FCSTD DOCUMENT  (FreeCAD 1.0RUnknown)
Label: wardrobe_jan_assy4
License: All rights reserved
objects: Measure::MeasureDistance×10, App::Link×5, App::DocumentObjectGroup×4, Measure::MeasureLength×2, PartDesign::CoordinateSystem×1, App::FeaturePython×1, App::Part×1
note: 1 computed .brp shape members not serialized (recipe doc carries the construction recipe); baked Part::Feature solids carry a one-line shape summary decoded from their .brp
EXTERNAL_REF file=room_corner_chimney_left.FCStd obj=LCS_1
EXTERNAL_REF file=room_corner_chimney_left.FCStd obj=Body010
EXTERNAL_REF file=mastersketch.FCStd obj=Spreadsheet
EXTERNAL_REF file=room_corner_chimney_left.FCStd obj=LCS_inner
EXTERNAL_REF file=subassemblies/wardrobe_corpus00_jan_assy4.FCStd obj=LCS_Origin
EXTERNAL_REF file=subassemblies/wardrobe_corpus00_jan_assy4.FCStd obj=Assembly
EXTERNAL_REF file=subassemblies/wardrobe_corpus01_jan_assy4.FCStd obj=LCS_Origin
EXTERNAL_REF file=subassemblies/wardrobe_corpus01_jan_assy4.FCStd obj=Assembly
EXTERNAL_REF file=subassemblies/wardrobe_corpus02_jan_assy4.FCStd obj=LCS_Origin
EXTERNAL_REF file=subassemblies/wardrobe_corpus02_jan_assy4.FCStd obj=Assembly
EXTERNAL_REF file=subassemblies/wardrobe_corpus03_jan_assy4.FCStd obj=LCS_Origin
EXTERNAL_REF file=subassemblies/wardrobe_corpus03_jan_assy4.FCStd obj=Assembly

FEATURE [App::DocumentObjectGroup] Parts
FEATURE [PartDesign::CoordinateSystem] LCS_Origin
  AttacherType = Attacher::AttachEngine3D
  AttachmentSupport = -> [X_Axis]
  MapMode = 2
FEATURE [App::DocumentObjectGroup] Constraints
FEATURE [App::FeaturePython] Variables  # WARN: FeaturePython — macro-defined, semantics opaque (R4)
  Type = App::PropertyContainer
FEATURE [App::DocumentObjectGroup] Configurations
FEATURE [App::Link] wall
  AttachedBy = #LCS_1
  AttachedTo = Parent Assembly#LCS_Origin
  LinkPlacement = pos=(330,-1080,10) rot=(0,0,-1;1.5708rad)
  LinkedObject = -> <external room_corner_chimney_left.FCStd>#Body010
  Placement = pos=(330,-1080,10) rot=(0,0,-1;1.5708rad)
  SolverId = Asm4EE
  expr: Placement = LCS_Origin.Placement * AttachmentOffset * room_corner_chimney_left#LCS_1.Placement ^ -1
FEATURE [App::Link] wardrobe_corpus00_jan
  AttachedBy = #LCS_Origin
  AttachedTo = wall#LCS_inner
  AttachmentOffset = pos=(280,30,-320) rot=(0,-0.707107,-0.707107;3.14159rad)
  LinkPlacement = pos=(10,-800,40) rot=(0,0,-1;1.5708rad)
  LinkedObject = -> <external subassemblies/wardrobe_corpus00_jan_assy4.FCStd>#Assembly
  Placement = pos=(10,-800,40) rot=(0,0,-1;1.5708rad)
  SolverId = Asm4EE
  expr: .AttachmentOffset.Base.x = mastersketch#Spreadsheet.corpus_width / 2 + 10
  expr: .AttachmentOffset.Base.y = mastersketch#Spreadsheet.hettich_height
  expr: .AttachmentOffset.Base.z = (mastersketch#Spreadsheet.corpus_depth / 2 + 10) * -1 - 10
  expr: Placement = wall.Placement * room_corner_chimney_left#LCS_inner.Placement * AttachmentOffset * wardrobe_corpus00_jan_assy4#LCS_Origin.Placement ^ -1
FEATURE [App::Link] wardrobe_corpus01_jan
  AttachedBy = #LCS_Origin
  AttachedTo = wall#LCS_inner
  AttachmentOffset = pos=(820,30,-320) rot=(0,-0.707107,-0.707107;3.14159rad)
  LinkPlacement = pos=(10,-260,40) rot=(0,0,-1;1.5708rad)
  LinkedObject = -> <external subassemblies/wardrobe_corpus01_jan_assy4.FCStd>#Assembly
  Placement = pos=(10,-260,40) rot=(0,0,-1;1.5708rad)
  SolverId = Asm4EE
  expr: .AttachmentOffset.Base.x = mastersketch#Spreadsheet.corpus_width * 1.5 + 10
  expr: .AttachmentOffset.Base.y = mastersketch#Spreadsheet.hettich_height
  expr: .AttachmentOffset.Base.z = (mastersketch#Spreadsheet.corpus_depth / 2 + 10) * -1 - 10
  expr: Placement = wall.Placement * room_corner_chimney_left#LCS_inner.Placement * AttachmentOffset * wardrobe_corpus01_jan_assy4#LCS_Origin.Placement ^ -1
FEATURE [App::Link] wardrobe_corpus02_jan
  AttachedBy = #LCS_Origin
  AttachedTo = wall#LCS_inner
  AttachmentOffset = pos=(1360,30,-320) rot=(0,-0.707107,-0.707107;3.14159rad)
  LinkPlacement = pos=(10,280,40) rot=(0,0,-1;1.5708rad)
  LinkedObject = -> <external subassemblies/wardrobe_corpus02_jan_assy4.FCStd>#Assembly
  Placement = pos=(10,280,40) rot=(0,0,-1;1.5708rad)
  SolverId = Asm4EE
  expr: .AttachmentOffset.Base.x = mastersketch#Spreadsheet.corpus_width * 2.5 + 10
  expr: .AttachmentOffset.Base.y = mastersketch#Spreadsheet.hettich_height
  expr: .AttachmentOffset.Base.z = (mastersketch#Spreadsheet.corpus_depth / 2 + 10) * -1 - 10
  expr: Placement = wall.Placement * room_corner_chimney_left#LCS_inner.Placement * AttachmentOffset * wardrobe_corpus02_jan_assy4#LCS_Origin.Placement ^ -1
FEATURE [App::Link] wardrobe_corpus03_jan
  AttachedBy = #LCS_Origin
  AttachedTo = wall#LCS_inner
  AttachmentOffset = pos=(1890,30,-320) rot=(0,-0.707107,-0.707107;3.14159rad)
  LinkPlacement = pos=(10,810,40) rot=(0,0,-1;1.5708rad)
  LinkedObject = -> <external subassemblies/wardrobe_corpus03_jan_assy4.FCStd>#Assembly
  Placement = pos=(10,810,40) rot=(0,0,-1;1.5708rad)
  SolverId = Asm4EE
  expr: .AttachmentOffset.Base.y = mastersketch#Spreadsheet.hettich_height
  expr: Placement = wall.Placement * room_corner_chimney_left#LCS_inner.Placement * AttachmentOffset * wardrobe_corpus03_jan_assy4#LCS_Origin.Placement ^ -1
FEATURE [App::Part] Assembly  label="wardrobe_jan"
  AssemblyType = Part::Link
  Group = -> [LCS_Origin,Constraints,Variables,Configurations,wall,wardrobe_corpus00_jan,wardrobe_corpus01_jan,wardrobe_corpus02_jan,wardrobe_corpus03_jan]
  Origin = -> Origin
  Type = Assembly
FEATURE [Measure::MeasureDistance] Distance  label="Distance: 760,75 mm"
  Distance = 760.748
  DistanceX = 516
  DistanceY = 559
  DistanceZ = 9.24e-14
  Element1 = -> Assembly [wardrobe_corpus01_jan.wardrobe_door_corpus01_jan.Pad.Edge4]
  Element2 = -> Assembly [wardrobe_corpus00_jan.wardrobe_door_corpus00_jan.Pad.Edge13]
  Position1 = (-309,-527.5,40)
  Position2 = (-825,-1086.5,40)
FEATURE [Measure::MeasureDistance] Distance001  label="Distance001: 6,50 mm"
  Distance = 6.5
  DistanceX = 0
  DistanceY = 6.5
  DistanceZ = 0
  Element1 = -> Assembly [wardrobe_corpus00_jan.wardrobe_door_corpus00_jan.Pad.Edge4]
  Element2 = -> Assembly [wall.Pad.Face6]
  Position1 = (-290,-1086.5,40)
  Position2 = (-290,-1080,40)
FEATURE [Measure::MeasureDistance] Distance002  label="Distance002: 5,00 mm"
  Distance = 5
  DistanceX = 1.137e-13
  DistanceY = 5
  DistanceZ = 5.68e-14
  Element1 = -> Assembly [wardrobe_corpus02_jan.wardrobe_door_corpus02_jan.Pad.Edge4]
  Element2 = -> Assembly [wardrobe_corpus01_jan.wardrobe_door_corpus01_jan.Pad.Edge10]
  Position1 = (-309,12.5,40)
  Position2 = (-309,7.5,40)
FEATURE [Measure::MeasureLength] Length  label="Length: 2045,55 mm"
  Elements = -> [Assembly]
  Length = 2045.55
FEATURE [Measure::MeasureDistance] Distance003  label="Distance003: 535,00 mm"
  Distance = 535
  DistanceX = 535
  DistanceY = 2.274e-13
  DistanceZ = 8.53e-14
  Element1 = -> Assembly [wardrobe_corpus00_jan.wardrobe_door_corpus00_jan.Pad.Edge13]
  Element2 = -> Assembly [wardrobe_corpus00_jan.wardrobe_door_corpus00_jan.Pad.Edge4]
  Position1 = (-825,-1086.5,40)
  Position2 = (-290,-1086.5,40)
FEATURE [Measure::MeasureDistance] Distance004  label="Distance004: 535,00 mm"
  Distance = 535
  DistanceX = 2.274e-13
  DistanceY = 535
  DistanceZ = 5.68e-14
  Element1 = -> Assembly [wardrobe_corpus01_jan.wardrobe_door_corpus01_jan.Pad.Edge10]
  Element2 = -> Assembly [wardrobe_corpus01_jan.wardrobe_door_corpus01_jan.Pad.Edge4]
  Position1 = (-309,7.5,40)
  Position2 = (-309,-527.5,40)
FEATURE [Measure::MeasureDistance] Distance005  label="Distance005: 30,00 mm"
  Distance = 30
  DistanceX = 0
  DistanceY = 0
  DistanceZ = 30
  Element1 = -> Assembly [wall.Pad.Face2]
  Element2 = -> Assembly [wardrobe_corpus01_jan.wardrobe_door_corpus01_jan.Pad.Face4]
  Position1 = (-290,7.5,10)
  Position2 = (-290,7.5,40)
FEATURE [Measure::MeasureDistance] Distance006  label="Distance006: 30,00 mm"
  Distance = 30
  DistanceX = 0
  DistanceY = 0
  DistanceZ = 30
  Element1 = -> Assembly [wall.Pad.Face2]
  Element2 = -> Assembly [wardrobe_corpus00_jan.wardrobe_door_corpus00_jan.Pad.Face5]
  Position1 = (-340,-1080,10)
  Position2 = (-340,-1080,40)
FEATURE [Measure::MeasureLength] Length001  label="Length001: 2051,40 mm"
  Elements = -> [Assembly]
  Length = 2051.4
FEATURE [Measure::MeasureDistance] Distance007  label="Distance007: 257,94 mm"
  Distance = 257.938
  DistanceX = 152.892
  DistanceY = 207.5
  DistanceZ = 10
  Element1 = -> Assembly [wall.Pad.Face4]
  Element2 = -> Assembly [wardrobe_corpus00_jan.wardrobe_door_corpus00_jan.Pad.Face3]
  Position1 = (-340,-860,2490)
  Position2 = (-492.892,-1067.5,2480)
FEATURE [Measure::MeasureDistance] Distance008  label="Distance008: 10,00 mm"
  Distance = 10
  DistanceX = 0
  DistanceY = 7.60201
  DistanceZ = 6.49688
  Element1 = -> Assembly [wall.Pad.Face4]
  Element2 = -> Assembly [wardrobe_corpus01_jan.wardrobe_door_corpus01_jan.Pad.Face2]
  Position1 = (-290,15.102,1466.04)
  Position2 = (-290,7.5,1459.54)
FEATURE [Measure::MeasureDistance] Distance009  label="Distance009: 10,00 mm"
  Distance = 10
  DistanceX = 0
  DistanceY = 7.60201
  DistanceZ = 6.49688
  Element1 = -> Assembly [wall.Pad.Face4]
  Element2 = -> Assembly [wardrobe_corpus02_jan.wardrobe_door_corpus02_jan.Pad.Face2]
  Position1 = (-290,555.102,834.185)
  Position2 = (-290,547.5,827.688)
FEATURE [App::DocumentObjectGroup] Measurements
  Group = -> [Distance,Distance001,Distance002,Length,Distance003,Distance004,Distance005,Distance006,Length001,Distance007,Distance008,Distance009]

RESOLVED EXTERNAL PARTS (link-assembly join: the EXTERNAL_REF files above that resolve inside this repo's crawl, each included once):
---- part mastersketch.FCStd = doc fcstd_204cd9ce44db ----
FCSTD DOCUMENT  (FreeCAD 1.0RUnknown)
Label: mastersketch
License: All rights reserved
LicenseURL: https://en.wikipedia.org/wiki/All_rights_reserved
objects: Sketcher::SketchObject×2, PartDesign::Body×1, Spreadsheet::Sheet×1
note: 5 computed .brp shape members not serialized (recipe doc carries the construction recipe); baked Part::Feature solids carry a one-line shape summary decoded from their .brp

FEATURE [Sketcher::SketchObject] Sketch  label="doors"
  ArcFitTolerance = 1e-06
  AttachmentSupport = -> [XZ_Plane]
  FullyConstrained = true
  MakeInternals = false
  MapMode = 5
  Placement = pos=(0,0,0) rot=(1,0,0;1.5708rad)
  expr: Constraints[23] = Spreadsheet.corpus_width - 5
  expr: Constraints[33] = Spreadsheet.hettich_height
  expr: Constraints[46] = Spreadsheet.corpus_width - 5
  expr: Constraints[58] = Spreadsheet.corpus_width - 5
  sketch-geometry (29):
    g0: LineSegment StartX=0 StartY=0 StartZ=0 EndX=0 EndY=2480 EndZ=0
    g1: LineSegment StartX=0 StartY=2480 StartZ=0 EndX=-220 EndY=2480 EndZ=0
    g2: LineSegment StartX=0 StartY=0 StartZ=0 EndX=-2160 EndY=0 EndZ=0
    g3: LineSegment StartX=-2160 StartY=0 StartZ=0 EndX=-2160 EndY=210 EndZ=0
    g4: LineSegment StartX=-2160 StartY=210 StartZ=0 EndX=-220 EndY=2480 EndZ=0
    g5: LineSegment StartX=-12.5 StartY=30 StartZ=0 EndX=-12.5 EndY=2081.4 EndZ=0
    g6: LineSegment StartX=-12.5 StartY=2081.4 StartZ=0 EndX=-547.5 EndY=2081.4 EndZ=0
    g7: LineSegment StartX=-547.5 StartY=2081.4 StartZ=0 EndX=-547.5 EndY=30 EndZ=0
    g8: LineSegment StartX=-547.5 StartY=30 StartZ=0 EndX=-12.5 EndY=30 EndZ=0
    g9: LineSegment StartX=-2160 StartY=194.608 StartZ=0 EndX=-206.846 EndY=2480 EndZ=0
    g10: LineSegment StartX=-2160 StartY=30 StartZ=0 EndX=0 EndY=30 EndZ=0
    g11: LineSegment StartX=-552.5 StartY=30 StartZ=0 EndX=-552.5 EndY=1449.54 EndZ=0
    g12: LineSegment StartX=-552.5 StartY=1449.54 StartZ=0 EndX=-1087.5 EndY=1449.54 EndZ=0
    g13: LineSegment StartX=-1087.5 StartY=1449.54 StartZ=0 EndX=-1087.5 EndY=30 EndZ=0
    g14: LineSegment StartX=-1087.5 StartY=30 StartZ=0 EndX=-552.5 EndY=30 EndZ=0
    g15: LineSegment StartX=-1627.5 StartY=30 StartZ=0 EndX=-1092.5 EndY=30 EndZ=0
    g16: LineSegment StartX=-1092.5 StartY=30 StartZ=0 EndX=-1092.5 EndY=817.688 EndZ=0
    g17: LineSegment StartX=-1092.5 StartY=817.688 StartZ=0 EndX=-1627.5 EndY=817.688 EndZ=0
    g18: LineSegment StartX=-1627.5 StartY=817.688 StartZ=0 EndX=-1627.5 EndY=30 EndZ=0
    g19: LineSegment StartX=-1632.5 StartY=811.837 StartZ=0 EndX=-1632.5 EndY=30 EndZ=0
    g20: LineSegment StartX=-12.5 StartY=2081.4 StartZ=0 EndX=-12.5 EndY=2470 EndZ=0
    g21: LineSegment StartX=-552.5 StartY=1449.54 StartZ=0 EndX=-552.5 EndY=2075.55 EndZ=0
    g22: LineSegment StartX=-1092.5 StartY=817.688 StartZ=0 EndX=-1092.5 EndY=1443.69 EndZ=0
    g23: LineSegment [constr] StartX=-12.5 StartY=2470 StartZ=0 EndX=-215.392 EndY=2470 EndZ=0
    g24: LineSegment [constr] StartX=-2147.5 StartY=209.234 StartZ=0 EndX=-2147.5 EndY=30 EndZ=0
    g25: LineSegment [constr] StartX=-2150 StartY=177.064 StartZ=0 EndX=-1627.5 EndY=788.443 EndZ=0
    g26: LineSegment [constr] StartX=-1904.57 StartY=493.489 StartZ=0 EndX=-1890.12 EndY=481.145 EndZ=0
    g27: LineSegment [constr] StartX=-2147.5 StartY=49 StartZ=0 EndX=-1627.5 EndY=49 EndZ=0
    g28: LineSegment [constr] StartX=-2150 StartY=177.064 StartZ=0 EndX=-2150 EndY=49 EndZ=0
  constraints (107):
    c: Distance(g0) = 2480
    c: Coincident(g0,g-1)
    c: PointOnObject(g0,g-2)
    c: Distance(g1) = 220
    c: Coincident(g1,g0)
    c: Horizontal(g1)
    c: Distance(g2) = 2160
    c: Coincident(g2,g0)
    c: PointOnObject(g2,g-1)
    c: Distance(g3) = 210
    c: Coincident(g3,g2)
    c: Vertical(g3)
    c: Coincident(g4,g3)
    c: Coincident(g4,g1)
    c: Coincident(g5,g6)
    c: Coincident(g6,g7)
    c: Coincident(g7,g8)
    c: Coincident(g8,g5)
    c: Vertical(g5)
    c: Vertical(g7)
    c: Horizontal(g6)
    c: Horizontal(g8)
    c: Distance(g0,g5) = 12.5
    c: DistanceX(g6,g6) = 535
    c: DistanceY(g5,g5) = 2051.4  'corpus00_height'
    c: PointOnObject(g9,g3)
    c: PointOnObject(g9,g1)
    c: Parallel(g4,g9)
    c: Distance(g3,g9) = 10
    c: PointOnObject(g6,g9)
    c: PointOnObject(g10,g3)
    c: PointOnObject(g10,g0)
    c: Horizontal(g10)
    c: Distance(g2,g10) = 30
    c: PointOnObject(g7,g10)
    c: Coincident(g11,g12)
    c: Coincident(g12,g13)
    c: Coincident(g13,g14)
    c: Coincident(g14,g11)
    c: Vertical(g11)
    c: Vertical(g13)
    c: Horizontal(g12)
    c: Horizontal(g14)
    c: PointOnObject(g11,g10)
    c: PointOnObject(g12,g9)
    c: Distance(g7,g11) = 5
    c: DistanceX(g12,g12) = 535
    c: Distance(g10,g12) = 1419.54  'corpus01_height'
    c: Coincident(g15,g16)
    c: Coincident(g16,g17)
    c: Coincident(g17,g18)
    c: Coincident(g18,g15)
    c: Horizontal(g15)
    c: Horizontal(g17)
    c: Vertical(g16)
    c: Vertical(g18)
    c: PointOnObject(g15,g10)
    c: PointOnObject(g17,g9)
    c: Distance(g16,g18) = 535
    c: Distance(g10,g17) = 787.688  'corpus02_height'
    c: Distance(g13,g16) = 5
    c: PointOnObject(g19,g9)
    c: PointOnObject(g19,g10)
    c: Vertical(g19)
    c: Distance(g18,g19) = 5
    c: DistanceY(g19,g19) = 781.837  'corpus03_door_height'
    c: Coincident(g20,g5)
    c: Vertical(g20)
    c: Distance(g20,g1) = 10
    c: Distance(g20,g8) = 2440  'corpus00_door_height'
    c: Coincident(g21,g11)
    c: Vertical(g21)
    c: Distance(g21,g10) = 2045.55  'corpus01_door_height'
    c: Coincident(g22,g16)
    c: Vertical(g22)
    c: PointOnObject(g21,g9)
    c: PointOnObject(g22,g9)
    c: Distance(g22,g10) = 1413.69  'corpus02_door_height'
    c: Angle(g3,g4) = 2.43442  'alpha'
    c: Distance(g6,g8) = 2051.4
    c: Coincident(g23,g20)
    c: PointOnObject(g23,g9)
    c: Horizontal(g23)
    c: DistanceX(g23,g23) = 202.892  'corpus00_door_top'
    c: PointOnObject(g24,g10)
    c: Vertical(g24)
    c: Distance(g3,g24) = 12.5
    c: Distance(g19,g24) = 515  'corpus03_door_width'
    c: PointOnObject(g25,g18)
    c: Parallel(g25,g9)
    c: PointOnObject(g26,g9)
    c: PointOnObject(g26,g25)
    c: Perpendicular(g25,g26)
    c: Distance(g26,g25) = 400
    c: Distance(g26,g26) = 19
    c: Distance(g25,g25) = 804.233  'corpus03_top'
    c: PointOnObject(g27,g24)
    c: PointOnObject(g27,g18)
    c: Horizontal(g27)
    c: Distance(g10,g27) = 19
    c: DistanceY(g27,g25) = 739.443  'corpus03_right_height'
    c: Vertical(g28)
    c: Horizontal(g28,g27)
    c: Distance(g28,g3) = 10
    c: DistanceY(g28,g28) = 128.064  'corpus03_left_height'
    c: Coincident(g28,g25)
    c: PointOnObject(g24,g9)
FEATURE [Sketcher::SketchObject] Sketch001  label="corpus"
  ArcFitTolerance = 1e-06
  AttachmentOffset = pos=(0,0,-20) rot=(0,0,1;0rad)
  AttachmentSupport = -> [XZ_Plane]
  ExternalGeometry = -> [Sketch]
  FullyConstrained = true
  MakeInternals = false
  MapMode = 5
  Placement = pos=(0,20,-4.4e-15) rot=(1,0,0;1.5708rad)
  expr: Constraints[22] = .Constraints.corpus_width
  expr: Constraints[33] = .Constraints.corpus_width
  expr: Constraints[55] = <<doors>>.Constraints.alpha
  expr: Constraints[65] = <<doors>>.Constraints.alpha
  sketch-geometry (29):
    g0: LineSegment StartX=-550 StartY=2078.47 StartZ=0 EndX=-550 EndY=30 EndZ=0
    g1: LineSegment StartX=-550 StartY=30 StartZ=0 EndX=-10 EndY=30 EndZ=0
    g2: LineSegment StartX=-10 StartY=30 StartZ=0 EndX=-10 EndY=2078.47 EndZ=0
    g3: LineSegment StartX=-10 StartY=2078.47 StartZ=0 EndX=-550 EndY=2078.47 EndZ=0
    g4: LineSegment StartX=-550 StartY=30 StartZ=0 EndX=-550 EndY=1446.62 EndZ=0
    g5: LineSegment StartX=-550 StartY=1446.62 StartZ=0 EndX=-1090 EndY=1446.62 EndZ=0
    g6: LineSegment StartX=-1090 StartY=1446.62 StartZ=0 EndX=-1090 EndY=30 EndZ=0
    g7: LineSegment StartX=-1090 StartY=30 StartZ=0 EndX=-550 EndY=30 EndZ=0
    g8: LineSegment StartX=-1090 StartY=30 StartZ=0 EndX=-1090 EndY=814.763 EndZ=0
    g9: LineSegment StartX=-1090 StartY=814.763 StartZ=0 EndX=-1630 EndY=814.763 EndZ=0
    g10: LineSegment StartX=-1630 StartY=814.763 StartZ=0 EndX=-1630 EndY=30 EndZ=0
    g11: LineSegment StartX=-1630 StartY=30 StartZ=0 EndX=-1090 EndY=30 EndZ=0
    g12: LineSegment StartX=-2150 StartY=30 StartZ=0 EndX=-1630 EndY=30 EndZ=0
    g13: LineSegment StartX=-1630 StartY=30 StartZ=0 EndX=-1630 EndY=49 EndZ=0
    g14: LineSegment StartX=-1630 StartY=49 StartZ=0 EndX=-2150 EndY=49 EndZ=0
    g15: LineSegment StartX=-2150 StartY=49 StartZ=0 EndX=-2150 EndY=30 EndZ=0
    g16: LineSegment StartX=-1649 StartY=49 StartZ=0 EndX=-1630 EndY=49 EndZ=0
    g17: LineSegment StartX=-1630 StartY=49 StartZ=0 EndX=-1630 EndY=785.518 EndZ=0
    g18: LineSegment StartX=-1649 StartY=763.286 StartZ=0 EndX=-1649 EndY=49 EndZ=0
    g19: LineSegment StartX=-1630 StartY=785.518 StartZ=0 EndX=-1649 EndY=763.286 EndZ=0
    g20: LineSegment StartX=-2150 StartY=49 StartZ=0 EndX=-2131 EndY=49 EndZ=0
    g21: LineSegment StartX=-2131 StartY=49 StartZ=0 EndX=-2131 EndY=199.296 EndZ=0
    g22: LineSegment StartX=-2150 StartY=177.064 StartZ=0 EndX=-2150 EndY=49 EndZ=0
    g23: LineSegment StartX=-2131 StartY=199.296 StartZ=0 EndX=-2150 EndY=177.064 EndZ=0
    g24: LineSegment StartX=-2150 StartY=177.064 StartZ=0 EndX=-2150 EndY=206.309 EndZ=0
    g25: LineSegment StartX=-2150 StartY=206.309 StartZ=0 EndX=-1630 EndY=814.763 EndZ=0
    g26: LineSegment StartX=-1630 StartY=814.763 StartZ=0 EndX=-1630 EndY=785.518 EndZ=0
    g27: LineSegment StartX=-1630 StartY=785.518 StartZ=0 EndX=-2150 EndY=177.064 EndZ=0
    g28: LineSegment [constr] StartX=-2150 StartY=206.309 StartZ=0 EndX=-2135.56 EndY=193.965 EndZ=0
  constraints (86):
    c: Coincident(g0,g1)
    c: Coincident(g1,g2)
    c: Coincident(g2,g3)
    c: Coincident(g3,g0)
    c: Vertical(g0)
    c: Vertical(g2)
    c: Horizontal(g1)
    c: Horizontal(g3)
    c: PointOnObject(g1,g-8)
    c: Distance(g-5,g2) = 10
    c: Distance(g2,g0) = 540  'corpus_width'
    c: Coincident(g4,g5)
    c: Coincident(g5,g6)
    c: Coincident(g6,g7)
    c: Coincident(g7,g4)
    c: Vertical(g4)
    c: Vertical(g6)
    c: Horizontal(g5)
    c: Horizontal(g7)
    c: Coincident(g4,g0)
    c: PointOnObject(g0,g-9)
    c: PointOnObject(g5,g-9)
    c: DistanceX(g6,g0) = 540
    c: Coincident(g8,g9)
    c: Coincident(g9,g10)
    c: Coincident(g10,g11)
    c: Coincident(g11,g8)
    c: Vertical(g8)
    c: Vertical(g10)
    c: Horizontal(g9)
    c: Horizontal(g11)
    c: Coincident(g8,g6)
    c: PointOnObject(g9,g-9)
    c: DistanceX(g10,g6) = 540
    c: Coincident(g12,g13)
    c: Coincident(g13,g14)
    c: Coincident(g14,g15)
    c: Coincident(g15,g12)
    c: Horizontal(g12)
    c: Horizontal(g14)
    c: Vertical(g13)
    c: Vertical(g15)
    c: PointOnObject(g12,g-8)
    c: PointOnObject(g13,g10)
    c: Distance(g12,g14) = 19
    c: DistanceX(g-8,g12) = 10
    c: Coincident(g16,g17)
    c: Coincident(g18,g16)
    c: Horizontal(g16)
    c: Vertical(g17)
    c: Vertical(g18)
    c: PointOnObject(g16,g14)
    c: PointOnObject(g17,g10)
    c: Coincident(g19,g17)
    c: Coincident(g18,g19)
    c: Angle(g18,g19) = 2.43442
    c: Distance(g16,g13) = 19
    c: Coincident(g20,g21)
    c: Coincident(g22,g20)
    c: Horizontal(g20)
    c: Vertical(g21)
    c: Vertical(g22)
    c: Coincident(g20,g14)
    c: Coincident(g23,g21)
    c: Coincident(g22,g23)
    c: Angle(g22,g23) = 2.43442
    c: Distance(g14,g20) = 19
    c: Coincident(g24,g22)
    c: Vertical(g24)
    c: Coincident(g25,g24)
    c: PointOnObject(g25,g10)
    c: Coincident(g26,g25)
    c: Coincident(g26,g17)
    c: Coincident(g27,g17)
    c: Coincident(g27,g22)
    c: Parallel(g27,g25)
    c: Parallel(g25,g-9)
    c: Coincident(g28,g24)
    c: PointOnObject(g28,g23)
    c: Perpendicular(g27,g28)
    c: Distance(g28,g28) = 19
    c: PointOnObject(g25,g-9)
    c: DistanceY(g13,g17) = 736.518  'corpus03_right_height'
    c: DistanceY(g22,g22) = 128.064  'corpus03_left_height'
    c: DistanceY(g10,g9) = 784.763  'corpus03_back_height'
    c: DistanceX(g14,g10) = 520  'corpus03_width'
FEATURE [PartDesign::Body] Body
  AllowCompound = false
  Group = -> [Sketch,Sketch001]
  Origin = -> Origin
FEATURE [Spreadsheet::Sheet] Spreadsheet
  cells = A1='corpus_width; B1(corpus_width)=540; A2='corpus_depth; B2(corpus_depth)=600; A3='corpus_outer_thickness; B3(corpus_outer_thickness)=19; A4='corpus_backplate_thickness; B4(corpus_backplate_thickness)=19; A5='corpus_heigth; B5(corpus_height)=2045; A6='corpus01_heigth; B6(corpus01_height)=1415; A7='corpus02_heigth; B7(corpus02_height)=780; A8='drawer_outer_thickness; B8(drawer_outer_thickness)=19; A9='drawer_bottom_thickness; B9(drawer_bottom_thickness)=6; A10='drawer_length; B10(drawer_length)==B2 - 50; A11='drawer_width; B11(drawer_width)==B1 - 2 * 12.5 - 2 * B3; A12='drawer_bottom_tol; B12(drawer_bottom_tol)=0.5; A13='drawer_height; B13(drawer_height)=170; A14='drawer_slot_depth; B14(drawer_slot_depth)=8; A15='drawer_slot_height; B15(drawer_slot_height)=10; A16='hettich_height; B16(hettich_height)=30
---- part room_corner_chimney_left.FCStd = doc fcstd_721c1199e5e2 ----
FCSTD DOCUMENT  (FreeCAD 1.0RUnknown)
Label: room_corner_chimney_left
License: All rights reserved
LicenseURL: https://en.wikipedia.org/wiki/All_rights_reserved
objects: Sketcher::SketchObject×2, PartDesign::Pad×2, PartDesign::CoordinateSystem×2, PartDesign::Body×1
note: 13 computed .brp shape members not serialized (recipe doc carries the construction recipe); baked Part::Feature solids carry a one-line shape summary decoded from their .brp

FEATURE [Sketcher::SketchObject] Sketch010
  ArcFitTolerance = 1e-06
  AttachmentSupport = -> [XZ_Plane013]
  FullyConstrained = true
  MakeInternals = false
  MapMode = 5
  Placement = pos=(0,0,0) rot=(1,0,0;1.5708rad)
  sketch-geometry (10):
    g0: LineSegment StartX=0 StartY=0 StartZ=0 EndX=-2160 EndY=0 EndZ=0
    g1: LineSegment StartX=-2160 StartY=0 StartZ=0 EndX=-2160 EndY=210 EndZ=0
    g2: LineSegment StartX=0 StartY=0 StartZ=0 EndX=0 EndY=2480 EndZ=0
    g3: LineSegment StartX=0 StartY=2480 StartZ=0 EndX=-220 EndY=2480 EndZ=0
    g4: LineSegment StartX=-2160 StartY=210 StartZ=0 EndX=-220 EndY=2480 EndZ=0
    g5: LineSegment StartX=-2170 StartY=213.691 StartZ=0 EndX=-224.608 EndY=2490 EndZ=0
    g6: LineSegment StartX=10 StartY=2490 StartZ=0 EndX=-224.608 EndY=2490 EndZ=0
    g7: LineSegment StartX=10 StartY=-10 StartZ=0 EndX=10 EndY=2490 EndZ=0
    g8: LineSegment StartX=10 StartY=-10 StartZ=0 EndX=-2170 EndY=-10 EndZ=0
    g9: LineSegment StartX=-2170 StartY=-10 StartZ=0 EndX=-2170 EndY=213.691 EndZ=0
  constraints (23):
    c: Distance(g0) = 2160
    c: Coincident(g0,g-1)
    c: Horizontal(g0)
    c: Distance(g1) = 210
    c: Coincident(g1,g0)
    c: Vertical(g1)
    c: Distance(g2) = 2480
    c: Coincident(g2,g0)
    c: PointOnObject(g2,g-2)
    c: Distance(g3) = 220
    c: Coincident(g3,g2)
    c: Horizontal(g3)
    c: Coincident(g4,g1)
    c: Coincident(g4,g3)
    c: Coincident(g5,g6)
    c: Coincident(g5,g9)
    c: Coincident(g6,g7)
    c: Coincident(g7,g8)
    c: Coincident(g8,g9)
    c: Block(g5)
    c: Block(g6)
    c: Block(g7)
    c: Block(g8)
FEATURE [PartDesign::Pad] Pad010
  Direction = (0,-1,2e-16)
  Length = 670
  Length2 = 10
  Placement = pos=(0,0,0) rot=(1,0,0;1.5708rad)
  Profile = -> Sketch010
  ReferenceAxis = -> Sketch010 [N_Axis]
  Refine = true
  Suppressed = false
  Type = 0
FEATURE [Sketcher::SketchObject] Sketch
  ArcFitTolerance = 1e-06
  AttachmentSupport = -> [Pad010]
  ExternalGeometry = -> [Pad010]
  FullyConstrained = true
  MakeInternals = false
  MapMode = 5
  Placement = pos=(0,2.111e-13,0) rot=(-1,0,0;1.5708rad)
  sketch-geometry (5):
    g0: LineSegment StartX=10 StartY=-2490 StartZ=0 EndX=10 EndY=10 EndZ=0
    g1: LineSegment StartX=10 StartY=10 StartZ=0 EndX=-2170 EndY=10 EndZ=0
    g2: LineSegment StartX=-2170 StartY=10 StartZ=0 EndX=-2170 EndY=-213.691 EndZ=0
    g3: LineSegment StartX=-2170 StartY=-213.691 StartZ=0 EndX=-224.608 EndY=-2490 EndZ=0
    g4: LineSegment StartX=-224.608 StartY=-2490 StartZ=0 EndX=10 EndY=-2490 EndZ=0
  constraints (10):
    c: Coincident(g0,g-5)
    c: Coincident(g0,g-4)
    c: Coincident(g1,g0)
    c: Coincident(g1,g-7)
    c: Coincident(g2,g1)
    c: Coincident(g2,g-7)
    c: Coincident(g3,g2)
    c: Coincident(g3,g-6)
    c: Coincident(g4,g3)
    c: Coincident(g4,g0)
FEATURE [PartDesign::Pad] Pad
  BaseFeature = -> Pad010
  Direction = (0,1,2e-16)
  Length = 10
  Length2 = 10
  Placement = pos=(0,0,0) rot=(1,0,0;1.5708rad)
  Profile = -> Sketch
  ReferenceAxis = -> Sketch [N_Axis]
  Refine = true
  Suppressed = false
  Type = 0
FEATURE [PartDesign::CoordinateSystem] LCS_1
  AttacherType = Attacher::AttachEngine3D
  AttachmentSupport = -> [Pad]
  MapMode = 45
  Placement = pos=(-1080,-330,-10) rot=(0,0,1;1.5708rad)
FEATURE [PartDesign::CoordinateSystem] LCS_inner
  AttacherType = Attacher::AttachEngine3D
  AttachmentSupport = -> [Pad]
  MapMode = 7
  Placement = pos=(0,0,0) rot=(0,0.707107,0.707107;3.14159rad)
FEATURE [PartDesign::Body] Body010  label="wall"
  AllowCompound = false
  Group = -> [Sketch010,Pad010,Sketch,Pad,LCS_1,LCS_inner]
  Origin = -> Origin013
  Tip = -> Pad
---- part subassemblies/wardrobe_corpus00_jan_assy4.FCStd = doc fcstd_f454c633ce21 ----
FCSTD DOCUMENT  (FreeCAD 1.0RUnknown)
Label: wardrobe_corpus00_jan_assy4
License: All rights reserved
objects: App::Link×8, App::DocumentObjectGroup×3, Part::FeaturePython×3, PartDesign::CoordinateSystem×2, App::FeaturePython×1, App::Part×1
note: 5 computed .brp shape members not serialized (recipe doc carries the construction recipe); baked Part::Feature solids carry a one-line shape summary decoded from their .brp
EXTERNAL_REF file=parts/wardrobe_base_jan.FCStd obj=LCS_center
EXTERNAL_REF file=parts/wardrobe_base_jan.FCStd obj=Body
EXTERNAL_REF file=parts/wardrobe_base_jan.FCStd obj=LCS_1
EXTERNAL_REF file=parts/wardrobe_left_corpus00_jan.FCStd obj=LCS_bottom
EXTERNAL_REF file=parts/wardrobe_left_corpus00_jan.FCStd obj=Body001
EXTERNAL_REF file=parts/wardrobe_base_jan.FCStd obj=LCS_right
EXTERNAL_REF file=parts/wardrobe_right_corpus00_jan.FCStd obj=LCS_bottom
EXTERNAL_REF file=parts/wardrobe_right_corpus00_jan.FCStd obj=Body002
EXTERNAL_REF file=parts/wardrobe_left_corpus00_jan.FCStd obj=LCS_top
EXTERNAL_REF file=parts/wardrobe_top_jan.FCStd obj=LCS_left
EXTERNAL_REF file=parts/wardrobe_top_jan.FCStd obj=Body003
EXTERNAL_REF file=parts/wardrobe_backplate_corpus00_jan.FCStd obj=LCS_bottom
EXTERNAL_REF file=parts/wardrobe_base_jan.FCStd obj=LCS_back
EXTERNAL_REF file=parts/wardrobe_backplate_corpus00_jan.FCStd obj=Body004
EXTERNAL_REF file=parts/wardrobe_base_jan.FCStd obj=LCS_door
EXTERNAL_REF file=parts/wardrobe_door_corpus00_jan.FCStd obj=Body
EXTERNAL_REF file=wardrobe_drawer_jan_assy4.FCStd obj=LCS_Origin
EXTERNAL_REF file=parts/wardrobe_left_corpus00_jan.FCStd obj=LCS_inner_bottom
EXTERNAL_REF file=wardrobe_drawer_jan_assy4.FCStd obj=Assembly
EXTERNAL_REF file=../purchased parts/hettich-level-adjustment.FCStd obj=LCS_Origin
EXTERNAL_REF file=parts/wardrobe_base_jan.FCStd obj=LCS_2
EXTERNAL_REF file=../purchased parts/hettich-level-adjustment.FCStd obj=hettich_level_adjustment

FEATURE [App::DocumentObjectGroup] Parts
FEATURE [PartDesign::CoordinateSystem] LCS_Origin
  AttacherType = Attacher::AttachEngine3D
  AttachmentSupport = -> [X_Axis]
  MapMode = 2
FEATURE [App::DocumentObjectGroup] Constraints
FEATURE [App::FeaturePython] Variables  # WARN: FeaturePython — macro-defined, semantics opaque (R4)
  Type = App::PropertyContainer
FEATURE [App::DocumentObjectGroup] Configurations
FEATURE [App::Link] wardrobe_base_jan
  AttachedBy = #LCS_center
  AttachedTo = Parent Assembly#LCS_Origin
  LinkedObject = -> <external parts/wardrobe_base_jan.FCStd>#Body
  SolverId = Asm4EE
  expr: Placement = LCS_Origin.Placement * AttachmentOffset * wardrobe_base_jan#LCS_center.Placement ^ -1
FEATURE [App::Link] wardrobe_left_corpus00_jan
  AttachedBy = #LCS_bottom
  AttachedTo = wardrobe_base_jan#LCS_1
  LinkPlacement = pos=(-270,2.37e-13,1022.5) rot=(0,0,1;0rad)
  LinkedObject = -> <external parts/wardrobe_left_corpus00_jan.FCStd>#Body001
  Placement = pos=(-270,2.37e-13,1022.5) rot=(0,0,1;0rad)
  SolverId = Asm4EE
  expr: Placement = wardrobe_base_jan.Placement * wardrobe_base_jan#LCS_1.Placement * AttachmentOffset * wardrobe_left_corpus00_jan#LCS_bottom.Placement ^ -1
FEATURE [App::Link] wardrobe_right_corpus00_jan
  AttachedBy = #LCS_bottom
  AttachedTo = wardrobe_base_jan#LCS_right
  LinkPlacement = pos=(251,2.086e-13,1022.5) rot=(0,0,1;0rad)
  LinkedObject = -> <external parts/wardrobe_right_corpus00_jan.FCStd>#Body002
  Placement = pos=(251,2.086e-13,1022.5) rot=(0,0,1;0rad)
  SolverId = Asm4EE
  expr: Placement = wardrobe_base_jan.Placement * wardrobe_base_jan#LCS_right.Placement * AttachmentOffset * wardrobe_right_corpus00_jan#LCS_bottom.Placement ^ -1
FEATURE [App::Link] wardrobe_top_jan
  AttachedBy = #LCS_left
  AttachedTo = wardrobe_left_corpus00_jan#LCS_top
  LinkPlacement = pos=(-5.116e-13,3.858e-13,2026) rot=(0,0,1;0rad)
  LinkedObject = -> <external parts/wardrobe_top_jan.FCStd>#Body003
  Placement = pos=(-5.116e-13,3.858e-13,2026) rot=(0,0,1;0rad)
  SolverId = Asm4EE
  expr: Placement = wardrobe_left_corpus00_jan.Placement * wardrobe_left_corpus00_jan#LCS_top.Placement * AttachmentOffset * wardrobe_top_jan#LCS_left.Placement ^ -1
FEATURE [App::Link] wardrobe_backplate_corpus00_jan
  AttachedBy = #LCS_bottom
  AttachedTo = wardrobe_base_jan#LCS_back
  LinkPlacement = pos=(5.68e-14,319,1022.5) rot=(0,0,1;0rad)
  LinkedObject = -> <external parts/wardrobe_backplate_corpus00_jan.FCStd>#Body004
  Placement = pos=(5.68e-14,319,1022.5) rot=(0,0,1;0rad)
  SolverId = Asm4EE
  expr: Placement = wardrobe_base_jan.Placement * wardrobe_base_jan#LCS_back.Placement * AttachmentOffset * wardrobe_backplate_corpus00_jan#LCS_bottom.Placement ^ -1
FEATURE [App::Link] wardrobe_door_corpus00_jan
  AttachedBy = #LCS_right
  AttachedTo = wardrobe_base_jan#LCS_door
  AttachmentOffset = pos=(2.5,0,0) rot=(0,0,1;1.5708rad)
  LinkPlacement = pos=(267.5,-300,0) rot=(0.57735,0.57735,0.57735;2.0944rad)
  LinkedObject = -> <external parts/wardrobe_door_corpus00_jan.FCStd>#Body
  Placement = pos=(267.5,-300,0) rot=(0.57735,0.57735,0.57735;2.0944rad)
  SolverId = Asm4EE
  expr: Placement = wardrobe_base_jan.Placement * wardrobe_base_jan#LCS_door.Placement * AttachmentOffset * wardrobe_door_corpus00_jan#LCS_right.Placement ^ -1
FEATURE [App::Link] wardrobe_drawer_jan_assy4
  AttachedBy = #LCS_Origin
  AttachedTo = wardrobe_left_corpus00_jan#LCS_inner_bottom
  AttachmentOffset = pos=(0,20,0) rot=(0,0,1;1.5708rad)
  LinkPlacement = pos=(-251,2.232e-13,39) rot=(0.57735,0.57735,0.57735;4.18879rad)
  LinkedObject = -> <external wardrobe_drawer_jan_assy4.FCStd>#Assembly
  Placement = pos=(-251,2.232e-13,39) rot=(0.57735,0.57735,0.57735;4.18879rad)
  SolverId = Asm4EE
  expr: Placement = wardrobe_left_corpus00_jan.Placement * wardrobe_left_corpus00_jan#LCS_inner_bottom.Placement * AttachmentOffset * wardrobe_drawer_jan_assy4#LCS_Origin.Placement ^ -1
FEATURE [Part::FeaturePython] Linear_wardrobe_drawer_jan_assy4  # Draft array (typed FeaturePython)
  ArrayType = Linear Array
  Axis = -> Z_Axis
  AxisPlacement = pos=(0,0,0) rot=(0,0,1.73205;3.14159rad)
  Count = 6
  Index = 1
  LinearStep = 200
  PlacementList = 6 placements: arithmetic series from (-251,2.2323e-13,39) step (5.68434e-14,0,200) to (-251,2.2323e-13,1039)
  Placer = pos=(0,0,1000) rot=(0,0,1;0rad)
  ScaleList = (6) [(1,1,1),(1,1,1),(1,1,1),(1,1,1),(1,1,1),(1,1,1)]
  Scaler = 1
  ShowElement = false
  SourceObject = -> wardrobe_drawer_jan_assy4
  expr: .Placer.Base.z = LinearStep * Index
FEATURE [PartDesign::CoordinateSystem] LCS_003  label="LCS_1"
  AttacherType = Attacher::AttachEngine3D
FEATURE [App::Link] hettich_level_adjustment
  AttachedBy = #LCS_Origin
  AttachedTo = wardrobe_base_jan#LCS_2
  AttachmentOffset = pos=(0,0,0) rot=(0.707107,-0.707107,0;3.14159rad)
  LinkPlacement = pos=(-220,-230,0) rot=(0.707107,-0.707107,0;3.14159rad)
  LinkedObject = -> <external ../purchased parts/hettich-level-adjustment.FCStd>#hettich_level_adjustment
  Placement = pos=(-220,-230,0) rot=(0.707107,-0.707107,0;3.14159rad)
  SolverId = Asm4EE
  expr: Placement = wardrobe_base_jan.Placement * wardrobe_base_jan#LCS_2.Placement * AttachmentOffset * hettich_level_adjustment#LCS_Origin.Placement ^ -1
FEATURE [Part::FeaturePython] Linear_hettich_level_adjustment  # Draft array (typed FeaturePython)
  ArrayType = Linear Array
  Axis = -> X_Axis
  AxisPlacement = pos=(0,0,0) rot=(0.57735,0.57735,0.57735;2.0944rad)
  Count = 2
  Index = 1
  LinearStep = 440
  PlacementList = 2 placements: [(-220,-230,6.31089e-30),(220,-230,4.88498e-14)]
  Placer = pos=(0,0,440) rot=(0,0,1;0rad)
  ScaleList = (2) [(1,1,1),(1,1,1)]
  Scaler = 1
  ShowElement = false
  SourceObject = -> hettich_level_adjustment
  expr: .Placer.Base.z = LinearStep * Index
FEATURE [Part::FeaturePython] Linear_Linear_hettich_level_adjustment  # Draft array (typed FeaturePython)
  ArrayType = Linear Array
  Axis = -> Y_Axis
  AxisPlacement = pos=(0,0,0) rot=(1,1,1;4.18879rad)
  Count = 2
  Index = 1
  LinearStep = 460
  PlacementList = 2 placements: [(0,0,0),(5.10703e-14,460,-1.53211e-13)]
  Placer = pos=(0,0,460) rot=(0,0,1;0rad)
  ScaleList = (2) [(1,1,1),(1,1,1)]
  Scaler = 1
  ShowElement = false
  SourceObject = -> Linear_hettich_level_adjustment
  expr: .Placer.Base.z = LinearStep * Index
FEATURE [App::Part] Assembly  label="wardrobe_corpus00_jan"
  AssemblyType = Part::Link
  Group = -> [LCS_Origin,Constraints,Variables,Configurations,wardrobe_base_jan,wardrobe_left_corpus00_jan,wardrobe_right_corpus00_jan,wardrobe_top_jan,wardrobe_backplate_corpus00_jan,wardrobe_door_corpus00_jan,wardrobe_drawer_jan_assy4,Linear_wardrobe_drawer_jan_assy4,LCS_003,hettich_level_adjustment,Linear_hettich_level_adjustment,Linear_Linear_hettich_level_adjustment]
  Origin = -> Origin
  Type = Assembly
---- part subassemblies/wardrobe_corpus01_jan_assy4.FCStd = doc fcstd_6551963c7e1b ----
FCSTD DOCUMENT  (FreeCAD 1.0RUnknown)
Label: wardrobe_corpus01_jan_assy4
License: All rights reserved
objects: App::Link×8, App::DocumentObjectGroup×3, Part::FeaturePython×3, PartDesign::CoordinateSystem×1, App::FeaturePython×1, App::Part×1
note: 4 computed .brp shape members not serialized (recipe doc carries the construction recipe); baked Part::Feature solids carry a one-line shape summary decoded from their .brp
EXTERNAL_REF file=parts/wardrobe_base_jan.FCStd obj=LCS_center
EXTERNAL_REF file=parts/wardrobe_base_jan.FCStd obj=Body
EXTERNAL_REF file=parts/wardrobe_base_jan.FCStd obj=LCS_1
EXTERNAL_REF file=parts/wardrobe_left_corpus01_jan.FCStd obj=LCS_bottom
EXTERNAL_REF file=parts/wardrobe_left_corpus01_jan.FCStd obj=Body001
EXTERNAL_REF file=parts/wardrobe_base_jan.FCStd obj=LCS_right
EXTERNAL_REF file=parts/wardrobe_right_corpus01_jan.FCStd obj=LCS_bottom
EXTERNAL_REF file=parts/wardrobe_right_corpus01_jan.FCStd obj=Body002
EXTERNAL_REF file=parts/wardrobe_left_corpus01_jan.FCStd obj=LCS_top
EXTERNAL_REF file=parts/wardrobe_top_jan.FCStd obj=LCS_left
EXTERNAL_REF file=parts/wardrobe_top_jan.FCStd obj=Body003
EXTERNAL_REF file=parts/wardrobe_backplate_corpus01_jan.FCStd obj=LCS_bottom
EXTERNAL_REF file=parts/wardrobe_base_jan.FCStd obj=LCS_back
EXTERNAL_REF file=parts/wardrobe_backplate_corpus01_jan.FCStd obj=Body004
EXTERNAL_REF file=parts/wardrobe_base_jan.FCStd obj=LCS_door
EXTERNAL_REF file=parts/wardrobe_door_corpus01_jan.FCStd obj=Body
EXTERNAL_REF file=wardrobe_drawer_jan_assy4.FCStd obj=LCS_Origin
EXTERNAL_REF file=parts/wardrobe_left_corpus01_jan.FCStd obj=LCS_inner
EXTERNAL_REF file=wardrobe_drawer_jan_assy4.FCStd obj=Assembly
EXTERNAL_REF file=../purchased parts/hettich-level-adjustment.FCStd obj=LCS_Origin
EXTERNAL_REF file=parts/wardrobe_base_jan.FCStd obj=LCS_2
EXTERNAL_REF file=../purchased parts/hettich-level-adjustment.FCStd obj=hettich_level_adjustment

FEATURE [App::DocumentObjectGroup] Parts
FEATURE [PartDesign::CoordinateSystem] LCS_Origin
  AttacherType = Attacher::AttachEngine3D
  AttachmentSupport = -> [X_Axis]
  MapMode = 2
FEATURE [App::DocumentObjectGroup] Constraints
FEATURE [App::FeaturePython] Variables  # WARN: FeaturePython — macro-defined, semantics opaque (R4)
  Type = App::PropertyContainer
FEATURE [App::DocumentObjectGroup] Configurations
FEATURE [App::Link] wardrobe_base_jan
  AttachedBy = #LCS_center
  AttachedTo = Parent Assembly#LCS_Origin
  LinkedObject = -> <external parts/wardrobe_base_jan.FCStd>#Body
  SolverId = Asm4EE
  expr: Placement = LCS_Origin.Placement * AttachmentOffset * wardrobe_base_jan#LCS_center.Placement ^ -1
FEATURE [App::Link] wardrobe_left_corpus01_jan
  AttachedBy = #LCS_bottom
  AttachedTo = wardrobe_base_jan#LCS_1
  LinkPlacement = pos=(-270,1.102e-13,707.5) rot=(0,0,1;0rad)
  LinkedObject = -> <external parts/wardrobe_left_corpus01_jan.FCStd>#Body001
  Placement = pos=(-270,1.102e-13,707.5) rot=(0,0,1;0rad)
  SolverId = Asm4EE
  expr: Placement = wardrobe_base_jan.Placement * wardrobe_base_jan#LCS_1.Placement * AttachmentOffset * wardrobe_left_corpus01_jan#LCS_bottom.Placement ^ -1
FEATURE [App::Link] wardrobe_right_corpus01_jan
  AttachedBy = #LCS_bottom
  AttachedTo = wardrobe_base_jan#LCS_right
  LinkPlacement = pos=(251,8.18e-14,707.5) rot=(0,0,1;0rad)
  LinkedObject = -> <external parts/wardrobe_right_corpus01_jan.FCStd>#Body002
  Placement = pos=(251,8.18e-14,707.5) rot=(0,0,1;0rad)
  SolverId = Asm4EE
  expr: Placement = wardrobe_base_jan.Placement * wardrobe_base_jan#LCS_right.Placement * AttachmentOffset * wardrobe_right_corpus01_jan#LCS_bottom.Placement ^ -1
FEATURE [App::Link] wardrobe_top_jan
  AttachedBy = #LCS_left
  AttachedTo = wardrobe_left_corpus01_jan#LCS_top
  LinkPlacement = pos=(-3.979e-13,2.306e-13,1396) rot=(0,0,1;0rad)
  LinkedObject = -> <external parts/wardrobe_top_jan.FCStd>#Body003
  Placement = pos=(-3.979e-13,2.306e-13,1396) rot=(0,0,1;0rad)
  SolverId = Asm4EE
  expr: Placement = wardrobe_left_corpus01_jan.Placement * wardrobe_left_corpus01_jan#LCS_top.Placement * AttachmentOffset * wardrobe_top_jan#LCS_left.Placement ^ -1
FEATURE [App::Link] wardrobe_backplate_corpus01_jan
  AttachedBy = #LCS_bottom
  AttachedTo = wardrobe_base_jan#LCS_back
  AttachmentOffset = pos=(0,0,0) rot=(0,1,0;3.14159rad)
  LinkPlacement = pos=(-2.84e-14,300,707.5) rot=(0,0,1;3.14159rad)
  LinkedObject = -> <external parts/wardrobe_backplate_corpus01_jan.FCStd>#Body004
  Placement = pos=(-2.84e-14,300,707.5) rot=(0,0,1;3.14159rad)
  SolverId = Asm4EE
  expr: Placement = wardrobe_base_jan.Placement * wardrobe_base_jan#LCS_back.Placement * AttachmentOffset * wardrobe_backplate_corpus01_jan#LCS_bottom.Placement ^ -1
FEATURE [App::Link] wardrobe_door_corpus01_jan
  AttachedBy = #LCS_bottom
  AttachedTo = wardrobe_base_jan#LCS_door
  AttachmentOffset = pos=(2.5,0,0) rot=(0,0,1;3.14159rad)
  LinkPlacement = pos=(267.5,-300,0) rot=(1,0,0;1.5708rad)
  LinkedObject = -> <external parts/wardrobe_door_corpus01_jan.FCStd>#Body
  Placement = pos=(267.5,-300,0) rot=(1,0,0;1.5708rad)
  SolverId = Asm4EE
  expr: Placement = wardrobe_base_jan.Placement * wardrobe_base_jan#LCS_door.Placement * AttachmentOffset * wardrobe_door_corpus01_jan#LCS_bottom.Placement ^ -1
FEATURE [App::Link] wardrobe_drawer_jan_assy4
  AttachedBy = #LCS_Origin
  AttachedTo = wardrobe_left_corpus01_jan#LCS_inner
  AttachmentOffset = pos=(0,20,0) rot=(0,0,1;1.5708rad)
  LinkPlacement = pos=(-251,9.64e-14,39) rot=(0.57735,0.57735,0.57735;4.18879rad)
  LinkedObject = -> <external wardrobe_drawer_jan_assy4.FCStd>#Assembly
  Placement = pos=(-251,9.64e-14,39) rot=(0.57735,0.57735,0.57735;4.18879rad)
  SolverId = Asm4EE
  expr: Placement = wardrobe_left_corpus01_jan.Placement * wardrobe_left_corpus01_jan#LCS_inner.Placement * AttachmentOffset * wardrobe_drawer_jan_assy4#LCS_Origin.Placement ^ -1
FEATURE [Part::FeaturePython] Linear_wardrobe_drawer_jan_assy4  # Draft array (typed FeaturePython)
  ArrayType = Linear Array
  Axis = -> Z_Axis
  AxisPlacement = pos=(0,0,0) rot=(0,0,1.73205;3.14159rad)
  Count = 6
  Index = 1
  LinearStep = 200
  PlacementList = 6 placements: arithmetic series from (-251,9.643e-14,39) step (5.68434e-14,0,200) to (-251,9.643e-14,1039)
  Placer = pos=(0,0,1000) rot=(0,0,1;0rad)
  ScaleList = (6) [(1,1,1),(1,1,1),(1,1,1),(1,1,1),(1,1,1),(1,1,1)]
  Scaler = 1
  ShowElement = false
  SourceObject = -> wardrobe_drawer_jan_assy4
  expr: .Placer.Base.z = LinearStep * Index
FEATURE [App::Link] hettich_level_adjustment
  AttachedBy = #LCS_Origin
  AttachedTo = wardrobe_base_jan#LCS_2
  AttachmentOffset = pos=(0,0,0) rot=(0.707107,-0.707107,0;3.14159rad)
  LinkPlacement = pos=(-220,-230,0) rot=(0.707107,-0.707107,0;3.14159rad)
  LinkedObject = -> <external ../purchased parts/hettich-level-adjustment.FCStd>#hettich_level_adjustment
  Placement = pos=(-220,-230,0) rot=(0.707107,-0.707107,0;3.14159rad)
  SolverId = Asm4EE
  expr: Placement = wardrobe_base_jan.Placement * wardrobe_base_jan#LCS_2.Placement * AttachmentOffset * hettich_level_adjustment#LCS_Origin.Placement ^ -1
FEATURE [Part::FeaturePython] Linear_hettich_level_adjustment  # Draft array (typed FeaturePython)
  ArrayType = Linear Array
  Axis = -> X_Axis
  AxisPlacement = pos=(0,0,0) rot=(0.57735,0.57735,0.57735;2.0944rad)
  Count = 2
  Index = 1
  LinearStep = 440
  PlacementList = 2 placements: [(-220,-230,6.31089e-30),(220,-230,4.88498e-14)]
  Placer = pos=(0,0,440) rot=(0,0,1;0rad)
  ScaleList = (2) [(1,1,1),(1,1,1)]
  Scaler = 1
  ShowElement = false
  SourceObject = -> hettich_level_adjustment
  expr: .Placer.Base.z = LinearStep * Index
FEATURE [Part::FeaturePython] Linear_Linear_hettich_level_adjustment  # Draft array (typed FeaturePython)
  ArrayType = Linear Array
  Axis = -> Y_Axis
  AxisPlacement = pos=(0,0,0) rot=(1,1,1;4.18879rad)
  Count = 2
  Index = 1
  LinearStep = 460
  PlacementList = 2 placements: [(0,0,0),(5.10703e-14,460,-1.53211e-13)]
  Placer = pos=(0,0,460) rot=(0,0,1;0rad)
  ScaleList = (2) [(1,1,1),(1,1,1)]
  Scaler = 1
  ShowElement = false
  SourceObject = -> Linear_hettich_level_adjustment
  expr: .Placer.Base.z = LinearStep * Index
FEATURE [App::Part] Assembly  label="wardrobe_corpus01_jan"
  AssemblyType = Part::Link
  Group = -> [LCS_Origin,Constraints,Variables,Configurations,wardrobe_base_jan,wardrobe_left_corpus01_jan,wardrobe_right_corpus01_jan,wardrobe_top_jan,wardrobe_backplate_corpus01_jan,wardrobe_door_corpus01_jan,wardrobe_drawer_jan_assy4,Linear_wardrobe_drawer_jan_assy4,hettich_level_adjustment,Linear_hettich_level_adjustment,Linear_Linear_hettich_level_adjustment]
  Origin = -> Origin
  Type = Assembly
---- part subassemblies/wardrobe_corpus02_jan_assy4.FCStd = doc fcstd_7aecd55c14e2 ----
FCSTD DOCUMENT  (FreeCAD 1.0RUnknown)
Label: wardrobe_corpus02_jan_assy4
License: All rights reserved
objects: App::Link×7, App::DocumentObjectGroup×3, Part::FeaturePython×2, PartDesign::CoordinateSystem×1, App::FeaturePython×1, App::Part×1
note: 3 computed .brp shape members not serialized (recipe doc carries the construction recipe); baked Part::Feature solids carry a one-line shape summary decoded from their .brp
EXTERNAL_REF file=parts/wardrobe_base_jan.FCStd obj=LCS_center
EXTERNAL_REF file=parts/wardrobe_base_jan.FCStd obj=Body
EXTERNAL_REF file=parts/wardrobe_base_jan.FCStd obj=LCS_1
EXTERNAL_REF file=parts/wardrobe_left_corpus02_jan.FCStd obj=LCS_1
EXTERNAL_REF file=parts/wardrobe_left_corpus02_jan.FCStd obj=Body001
EXTERNAL_REF file=parts/wardrobe_base_jan.FCStd obj=LCS_right
EXTERNAL_REF file=parts/wardrobe_right_corpus02_jan.FCStd obj=LCS_1
EXTERNAL_REF file=parts/wardrobe_right_corpus02_jan.FCStd obj=Body002
EXTERNAL_REF file=parts/wardrobe_left_corpus02_jan.FCStd obj=LCS_top
EXTERNAL_REF file=parts/wardrobe_top_jan.FCStd obj=LCS_left
EXTERNAL_REF file=parts/wardrobe_top_jan.FCStd obj=Body003
EXTERNAL_REF file=parts/wardrobe_backplate_corpus02_jan.FCStd obj=LCS_1
EXTERNAL_REF file=parts/wardrobe_base_jan.FCStd obj=LCS_back
EXTERNAL_REF file=parts/wardrobe_backplate_corpus02_jan.FCStd obj=Body004
EXTERNAL_REF file=parts/wardrobe_base_jan.FCStd obj=LCS_door
EXTERNAL_REF file=parts/wardrobe_door_corpus02_jan.FCStd obj=LCS_1
EXTERNAL_REF file=parts/wardrobe_door_corpus02_jan.FCStd obj=Body
EXTERNAL_REF file=../purchased parts/hettich-level-adjustment.FCStd obj=LCS_Origin
EXTERNAL_REF file=parts/wardrobe_base_jan.FCStd obj=LCS_2
EXTERNAL_REF file=../purchased parts/hettich-level-adjustment.FCStd obj=hettich_level_adjustment

FEATURE [App::DocumentObjectGroup] Parts
FEATURE [PartDesign::CoordinateSystem] LCS_Origin
  AttacherType = Attacher::AttachEngine3D
  AttachmentSupport = -> [X_Axis]
  MapMode = 2
FEATURE [App::DocumentObjectGroup] Constraints
FEATURE [App::FeaturePython] Variables  # WARN: FeaturePython — macro-defined, semantics opaque (R4)
  Type = App::PropertyContainer
FEATURE [App::DocumentObjectGroup] Configurations
FEATURE [App::Link] wardrobe_base_jan
  AttachedBy = #LCS_center
  AttachedTo = Parent Assembly#LCS_Origin
  LinkedObject = -> <external parts/wardrobe_base_jan.FCStd>#Body
  SolverId = Asm4EE
  expr: Placement = LCS_Origin.Placement * AttachmentOffset * wardrobe_base_jan#LCS_center.Placement ^ -1
FEATURE [App::Link] wardrobe_left_corpus02_jan
  AttachedBy = #LCS_1
  AttachedTo = wardrobe_base_jan#LCS_1
  LinkPlacement = pos=(-270,1.25e-13,390) rot=(0,0,1;0rad)
  LinkedObject = -> <external parts/wardrobe_left_corpus02_jan.FCStd>#Body001
  Placement = pos=(-270,1.25e-13,390) rot=(0,0,1;0rad)
  SolverId = Asm4EE
  expr: Placement = wardrobe_base_jan.Placement * wardrobe_base_jan#LCS_1.Placement * AttachmentOffset * wardrobe_left_corpus02_jan#LCS_1.Placement ^ -1
FEATURE [App::Link] wardrobe_right_corpus02_jan
  AttachedBy = #LCS_1
  AttachedTo = wardrobe_base_jan#LCS_right
  LinkPlacement = pos=(251,9.66e-14,390) rot=(0,0,1;0rad)
  LinkedObject = -> <external parts/wardrobe_right_corpus02_jan.FCStd>#Body002
  Placement = pos=(251,9.66e-14,390) rot=(0,0,1;0rad)
  SolverId = Asm4EE
  expr: Placement = wardrobe_base_jan.Placement * wardrobe_base_jan#LCS_right.Placement * AttachmentOffset * wardrobe_right_corpus02_jan#LCS_1.Placement ^ -1
FEATURE [App::Link] wardrobe_top_jan
  AttachedBy = #LCS_left
  AttachedTo = wardrobe_left_corpus02_jan#LCS_top
  LinkPlacement = pos=(-2.274e-13,1.885e-13,761) rot=(0,0,1;0rad)
  LinkedObject = -> <external parts/wardrobe_top_jan.FCStd>#Body003
  Placement = pos=(-2.274e-13,1.885e-13,761) rot=(0,0,1;0rad)
  SolverId = Asm4EE
  expr: Placement = wardrobe_left_corpus02_jan.Placement * wardrobe_left_corpus02_jan#LCS_top.Placement * AttachmentOffset * wardrobe_top_jan#LCS_left.Placement ^ -1
FEATURE [App::Link] wardrobe_backplate_corpus02_jan
  AttachedBy = #LCS_1
  AttachedTo = wardrobe_base_jan#LCS_back
  LinkPlacement = pos=(2.84e-14,319,390) rot=(0,0,1;0rad)
  LinkedObject = -> <external parts/wardrobe_backplate_corpus02_jan.FCStd>#Body004
  Placement = pos=(2.84e-14,319,390) rot=(0,0,1;0rad)
  SolverId = Asm4EE
  expr: Placement = wardrobe_base_jan.Placement * wardrobe_base_jan#LCS_back.Placement * AttachmentOffset * wardrobe_backplate_corpus02_jan#LCS_1.Placement ^ -1
FEATURE [App::Link] wardrobe_door_corpus02_jan
  AttachedBy = #LCS_1
  AttachedTo = wardrobe_base_jan#LCS_door
  AttachmentOffset = pos=(2.5,0,0) rot=(0,0,1;3.14159rad)
  LinkPlacement = pos=(267.5,-300,0) rot=(1,0,0;1.5708rad)
  LinkedObject = -> <external parts/wardrobe_door_corpus02_jan.FCStd>#Body
  Placement = pos=(267.5,-300,0) rot=(1,0,0;1.5708rad)
  SolverId = Asm4EE
  expr: Placement = wardrobe_base_jan.Placement * wardrobe_base_jan#LCS_door.Placement * AttachmentOffset * wardrobe_door_corpus02_jan#LCS_1.Placement ^ -1
FEATURE [App::Link] hettich_level_adjustment
  AttachedBy = #LCS_Origin
  AttachedTo = wardrobe_base_jan#LCS_2
  AttachmentOffset = pos=(0,0,0) rot=(0.707107,-0.707107,0;3.14159rad)
  LinkPlacement = pos=(-220,-230,0) rot=(0.707107,-0.707107,0;3.14159rad)
  LinkedObject = -> <external ../purchased parts/hettich-level-adjustment.FCStd>#hettich_level_adjustment
  Placement = pos=(-220,-230,0) rot=(0.707107,-0.707107,0;3.14159rad)
  SolverId = Asm4EE
  expr: Placement = wardrobe_base_jan.Placement * wardrobe_base_jan#LCS_2.Placement * AttachmentOffset * hettich_level_adjustment#LCS_Origin.Placement ^ -1
FEATURE [Part::FeaturePython] Linear_hettich_level_adjustment  # Draft array (typed FeaturePython)
  ArrayType = Linear Array
  Axis = -> X_Axis
  AxisPlacement = pos=(0,0,0) rot=(0.57735,0.57735,0.57735;2.0944rad)
  Count = 2
  Index = 1
  LinearStep = 440
  PlacementList = 2 placements: [(-220,-230,6.31089e-30),(220,-230,4.88498e-14)]
  Placer = pos=(0,0,440) rot=(0,0,1;0rad)
  ScaleList = (2) [(1,1,1),(1,1,1)]
  Scaler = 1
  ShowElement = false
  SourceObject = -> hettich_level_adjustment
  expr: .Placer.Base.z = LinearStep * Index
FEATURE [Part::FeaturePython] Linear_Linear_hettich_level_adjustment  # Draft array (typed FeaturePython)
  ArrayType = Linear Array
  Axis = -> Y_Axis
  AxisPlacement = pos=(0,0,0) rot=(1,1,1;4.18879rad)
  Count = 2
  Index = 1
  LinearStep = 460
  PlacementList = 2 placements: [(0,0,0),(5.10703e-14,460,-1.53211e-13)]
  Placer = pos=(0,0,460) rot=(0,0,1;0rad)
  ScaleList = (2) [(1,1,1),(1,1,1)]
  Scaler = 1
  ShowElement = false
  SourceObject = -> Linear_hettich_level_adjustment
  expr: .Placer.Base.z = LinearStep * Index
FEATURE [App::Part] Assembly  label="wardrobe_corpus02_jan"
  AssemblyType = Part::Link
  Group = -> [LCS_Origin,Constraints,Variables,Configurations,wardrobe_base_jan,wardrobe_left_corpus02_jan,wardrobe_right_corpus02_jan,wardrobe_top_jan,wardrobe_backplate_corpus02_jan,wardrobe_door_corpus02_jan,hettich_level_adjustment,Linear_hettich_level_adjustment,Linear_Linear_hettich_level_adjustment]
  Origin = -> Origin
  Type = Assembly
---- part subassemblies/wardrobe_corpus03_jan_assy4.FCStd = doc fcstd_4acb24734bf8 ----
FCSTD DOCUMENT  (FreeCAD 1.0RUnknown)
Label: wardrobe_corpus03_jan_assy4
License: All rights reserved
LicenseURL: https://en.wikipedia.org/wiki/All_rights_reserved
objects: App::Link×7, App::DocumentObjectGroup×3, Part::FeaturePython×2, PartDesign::CoordinateSystem×1, App::FeaturePython×1, App::Part×1, Assembly::BomObject×1
note: 3 computed .brp shape members not serialized (recipe doc carries the construction recipe); baked Part::Feature solids carry a one-line shape summary decoded from their .brp
EXTERNAL_REF file=parts/wardrobe_base_corpus03_jan.FCStd obj=LCS_Origin
EXTERNAL_REF file=parts/wardrobe_base_corpus03_jan.FCStd obj=wardrobe_base_corpus03_jan
EXTERNAL_REF file=parts/wardrobe_base_corpus03_jan.FCStd obj=LCS_1
EXTERNAL_REF file=parts/wardrobe_left_corpus03_jan.FCStd obj=LCS_1
EXTERNAL_REF file=parts/wardrobe_left_corpus03_jan.FCStd obj=wardrobe_left_corpus03_jan
EXTERNAL_REF file=parts/wardrobe_base_corpus03_jan.FCStd obj=LCS_right
EXTERNAL_REF file=parts/wardrobe_right_corpus03_jan.FCStd obj=LCS_1
EXTERNAL_REF file=parts/wardrobe_right_corpus03_jan.FCStd obj=wardrobe_right_corpus03_jan
EXTERNAL_REF file=parts/wardrobe_left_corpus03_jan.FCStd obj=LCS_2
EXTERNAL_REF file=parts/wardrobe_top_corpus03_jan.FCStd obj=LCS_1
EXTERNAL_REF file=parts/wardrobe_top_corpus03_jan.FCStd obj=wardrobe_top_corpus03_jan
EXTERNAL_REF file=../purchased parts/hettich-level-adjustment.FCStd obj=LCS_Origin
EXTERNAL_REF file=parts/wardrobe_base_corpus03_jan.FCStd obj=LCS_2
EXTERNAL_REF file=../purchased parts/hettich-level-adjustment.FCStd obj=hettich_level_adjustment
EXTERNAL_REF file=../mastersketch.FCStd obj=Sketch001
EXTERNAL_REF file=parts/wardrobe_backplate_corpus03_jan.FCStd obj=LCS_1
EXTERNAL_REF file=parts/wardrobe_base_corpus03_jan.FCStd obj=LCS_back
EXTERNAL_REF file=parts/wardrobe_backplate_corpus03_jan.FCStd obj=wardrobe_backplate_corpus03_jan
EXTERNAL_REF file=parts/wardrobe_base_corpus03_jan.FCStd obj=LCS_door
EXTERNAL_REF file=parts/wardrobe_door_03_jan.FCStd obj=LCS_Origin
EXTERNAL_REF file=parts/wardrobe_door_03_jan.FCStd obj=wardrobe_door_03_jan

FEATURE [App::DocumentObjectGroup] Parts
FEATURE [PartDesign::CoordinateSystem] LCS_Origin
  AttacherType = Attacher::AttachEngine3D
  AttachmentSupport = -> [X_Axis]
  MapMode = 2
FEATURE [App::DocumentObjectGroup] Constraints
FEATURE [App::FeaturePython] Variables  # WARN: FeaturePython — macro-defined, semantics opaque (R4)
  Type = App::PropertyContainer
FEATURE [App::DocumentObjectGroup] Configurations
FEATURE [App::Link] wardrobe_base_corpus03_jan001
  AttachedBy = #LCS_Origin
  AttachedTo = Parent Assembly#LCS_Origin
  LinkedObject = -> <external parts/wardrobe_base_corpus03_jan.FCStd>#wardrobe_base_corpus03_jan
  SolverId = Asm4EE
  expr: Placement = LCS_Origin.Placement * AttachmentOffset * wardrobe_base_corpus03_jan#LCS_Origin.Placement ^ -1
FEATURE [App::Link] wardrobe_left_corpus03_jan001
  AttachedBy = #LCS_1
  AttachedTo = wardrobe_base_corpus03_jan001#LCS_1
  AttachmentOffset = pos=(0,0,0) rot=(0,1,0;3.14159rad)
  LinkPlacement = pos=(-260,300,19) rot=(0,0,1;4.71239rad)
  LinkedObject = -> <external parts/wardrobe_left_corpus03_jan.FCStd>#wardrobe_left_corpus03_jan
  Placement = pos=(-260,300,19) rot=(0,0,1;4.71239rad)
  SolverId = Asm4EE
  expr: Placement = wardrobe_base_corpus03_jan001.Placement * wardrobe_base_corpus03_jan#LCS_1.Placement * AttachmentOffset * wardrobe_left_corpus03_jan#LCS_1.Placement ^ -1
FEATURE [App::Link] wardrobe_right_corpus03_jan001
  AttachedBy = #LCS_1
  AttachedTo = wardrobe_base_corpus03_jan001#LCS_right
  LinkPlacement = pos=(260,300,19) rot=(0,0,1;0rad)
  LinkedObject = -> <external parts/wardrobe_right_corpus03_jan.FCStd>#wardrobe_right_corpus03_jan
  Placement = pos=(260,300,19) rot=(0,0,1;0rad)
  SolverId = Asm4EE
  expr: Placement = wardrobe_base_corpus03_jan001.Placement * wardrobe_base_corpus03_jan#LCS_right.Placement * AttachmentOffset * wardrobe_right_corpus03_jan#LCS_1.Placement ^ -1
FEATURE [App::Link] wardrobe_top_corpus03_jan001
  AttachedBy = #LCS_1
  AttachedTo = wardrobe_left_corpus03_jan001#LCS_2
  AttachmentOffset = pos=(0,0,0) rot=(0,1,0;3.14159rad)
  LinkPlacement = pos=(5.68e-14,300,465.913) rot=(0,1,0;5.41956rad)
  LinkedObject = -> <external parts/wardrobe_top_corpus03_jan.FCStd>#wardrobe_top_corpus03_jan
  Placement = pos=(5.68e-14,300,465.913) rot=(0,1,0;5.41956rad)
  SolverId = Asm4EE
  expr: Placement = wardrobe_left_corpus03_jan001.Placement * wardrobe_left_corpus03_jan#LCS_2.Placement * AttachmentOffset * wardrobe_top_corpus03_jan#LCS_1.Placement ^ -1
FEATURE [App::Link] hettich_level_adjustment
  AttachedBy = #LCS_Origin
  AttachedTo = wardrobe_base_corpus03_jan001#LCS_2
  AttachmentOffset = pos=(0,0,0) rot=(0.707107,0.707107,0;3.14159rad)
  LinkPlacement = pos=(-220,-230,0) rot=(0.707107,0.707107,0;3.14159rad)
  LinkedObject = -> <external ../purchased parts/hettich-level-adjustment.FCStd>#hettich_level_adjustment
  Placement = pos=(-220,-230,0) rot=(0.707107,0.707107,0;3.14159rad)
  SolverId = Asm4EE
  expr: Placement = wardrobe_base_corpus03_jan001.Placement * wardrobe_base_corpus03_jan#LCS_2.Placement * AttachmentOffset * hettich_level_adjustment#LCS_Origin.Placement ^ -1
FEATURE [Part::FeaturePython] Linear_hettich_level_adjustment  # Draft array (typed FeaturePython)
  ArrayType = Linear Array
  Axis = -> X_Axis
  AxisPlacement = pos=(0,0,0) rot=(0.57735,0.57735,0.57735;2.0944rad)
  Count = 2
  Index = 1
  LinearStep = 440
  PlacementList = 2 placements: [(-220,-230,6.31089e-30),(220,-230,4.88498e-14)]
  Placer = pos=(0,0,440) rot=(0,0,1;0rad)
  ScaleList = (2) [(1,1,1),(1,1,1)]
  Scaler = 1
  ShowElement = false
  SourceObject = -> hettich_level_adjustment
  expr: .Placer.Base.z = LinearStep * Index
  expr: LinearStep = mastersketch#<<corpus>>.Constraints.corpus_width - 100 mm
FEATURE [Part::FeaturePython] Linear_Linear_hettich_level_adjustment  # Draft array (typed FeaturePython)
  ArrayType = Linear Array
  Axis = -> Y_Axis
  AxisPlacement = pos=(0,0,0) rot=(1,1,1;4.18879rad)
  Count = 2
  Index = 1
  LinearStep = 460
  PlacementList = 2 placements: [(0,0,0),(5.10703e-14,460,-1.53211e-13)]
  Placer = pos=(0,0,460) rot=(0,0,1;0rad)
  ScaleList = (2) [(1,1,1),(1,1,1)]
  Scaler = 1
  ShowElement = false
  SourceObject = -> Linear_hettich_level_adjustment
  expr: .Placer.Base.z = LinearStep * Index
FEATURE [App::Link] wardrobe_backplate_corpus03_jan001
  AttachedBy = #LCS_1
  AttachedTo = wardrobe_base_corpus03_jan001#LCS_back
  AttachmentOffset = pos=(0,0,0) rot=(0,0,1;1.5708rad)
  LinkPlacement = pos=(260,309,-1.4e-15) rot=(1,0,0;1.5708rad)
  LinkedObject = -> <external parts/wardrobe_backplate_corpus03_jan.FCStd>#wardrobe_backplate_corpus03_jan
  Placement = pos=(260,309,-1.4e-15) rot=(1,0,0;1.5708rad)
  SolverId = Asm4EE
  expr: Placement = wardrobe_base_corpus03_jan001.Placement * wardrobe_base_corpus03_jan#LCS_back.Placement * AttachmentOffset * wardrobe_backplate_corpus03_jan#LCS_1.Placement ^ -1
FEATURE [App::Link] wardrobe_door_03_jan
  AttachedBy = #LCS_Origin
  AttachedTo = wardrobe_base_corpus03_jan001#LCS_door
  AttachmentOffset = pos=(2.5,0,0) rot=(0,-0.707107,0.707107;3.14159rad)
  LinkPlacement = pos=(257.5,-300,0) rot=(1,0,0;1.5708rad)
  LinkedObject = -> <external parts/wardrobe_door_03_jan.FCStd>#wardrobe_door_03_jan
  Placement = pos=(257.5,-300,0) rot=(1,0,0;1.5708rad)
  SolverId = Asm4EE
  expr: Placement = wardrobe_base_corpus03_jan001.Placement * wardrobe_base_corpus03_jan#LCS_door.Placement * AttachmentOffset * wardrobe_door_03_jan#LCS_Origin.Placement ^ -1
FEATURE [App::Part] Assembly  label="wardrobe_corpus03_jan"
  AssemblyType = Part::Link
  DrawingName = wardrobe_corpus03_jan_assy4.FCStd
  Group = -> [LCS_Origin,Constraints,Variables,Configurations,wardrobe_base_corpus03_jan001,wardrobe_left_corpus03_jan001,wardrobe_right_corpus03_jan001,wardrobe_top_corpus03_jan001,hettich_level_adjustment,Linear_hettich_level_adjustment,Linear_Linear_hettich_level_adjustment,wardrobe_backplate_corpus03_jan001,wardrobe_door_03_jan]
  Origin = -> Origin
  PartID = wardrobe_corpus03_jan_assy4
  Type = Assembly
FEATURE [Assembly::BomObject] Bill_of_Materials
  cells = A1='Index; B1='Name; C1='Description; D1='File Name; E1='Quantity; A2='1; B2='wardrobe_corpus03_jan; D2='<userpath>/Projekte/attic-furniture/wardrobe_jan/subassemblies/wardrobe_corpus03_jan_assy4.FCStd; E2=1; A3='1.1; B3='wardrobe_base_corpus03_jan001; D3='<userpath>/Projekte/attic-furniture/wardrobe_jan/subassemblies/parts/wardrobe_base_corpus03_jan.FCStd; E3=1; A4='1.2; B4='wardrobe_left_corpus03_jan001; D4='<userpath>/Projekte/attic-furniture/wardrobe_jan/subassemblies/parts/wardrobe_left_corpus03_jan.FCStd; E4=1; A5='1.3; B5='wardrobe_right_corpus03_jan001; D5='<userpath>/Projekte/attic-furniture/wardrobe_jan/subassemblies/parts/wardrobe_right_corpus03_jan.FCStd; E5=1; A6='1.4; B6='wardrobe_top_corpus03_jan001; D6='<userpath>/Projekte/attic-furniture/wardrobe_jan/subassemblies/parts/wardrobe_top_corpus03_jan.FCStd; E6=1; A7='1.5; B7='hettich_level_adjustment; D7='<userpath>/Projekte/attic-furniture/wardrobe_jan/purchased parts/hettich-level-adjustment.FCStd; E7=1; A8='1.6; B8='wardrobe_backplate_corpus03_jan001; D8='<userpath>/Projekte/attic-furniture/wardrobe_jan/subassemblies/parts/wardrobe_backplate_corpus03_jan.FCStd; E8=1; A9='1.7; B9='wardrobe_door_03_jan; D9='<userpath>/Projekte/attic-furniture/wardrobe_jan/subassemblies/parts/wardrobe_door_03_jan.FCStd; E9=1
  columnsNames = Index | Name | Description | File Name | Quantity
  detailParts = true
  detailSubAssemblies = false
  onlyParts = true
